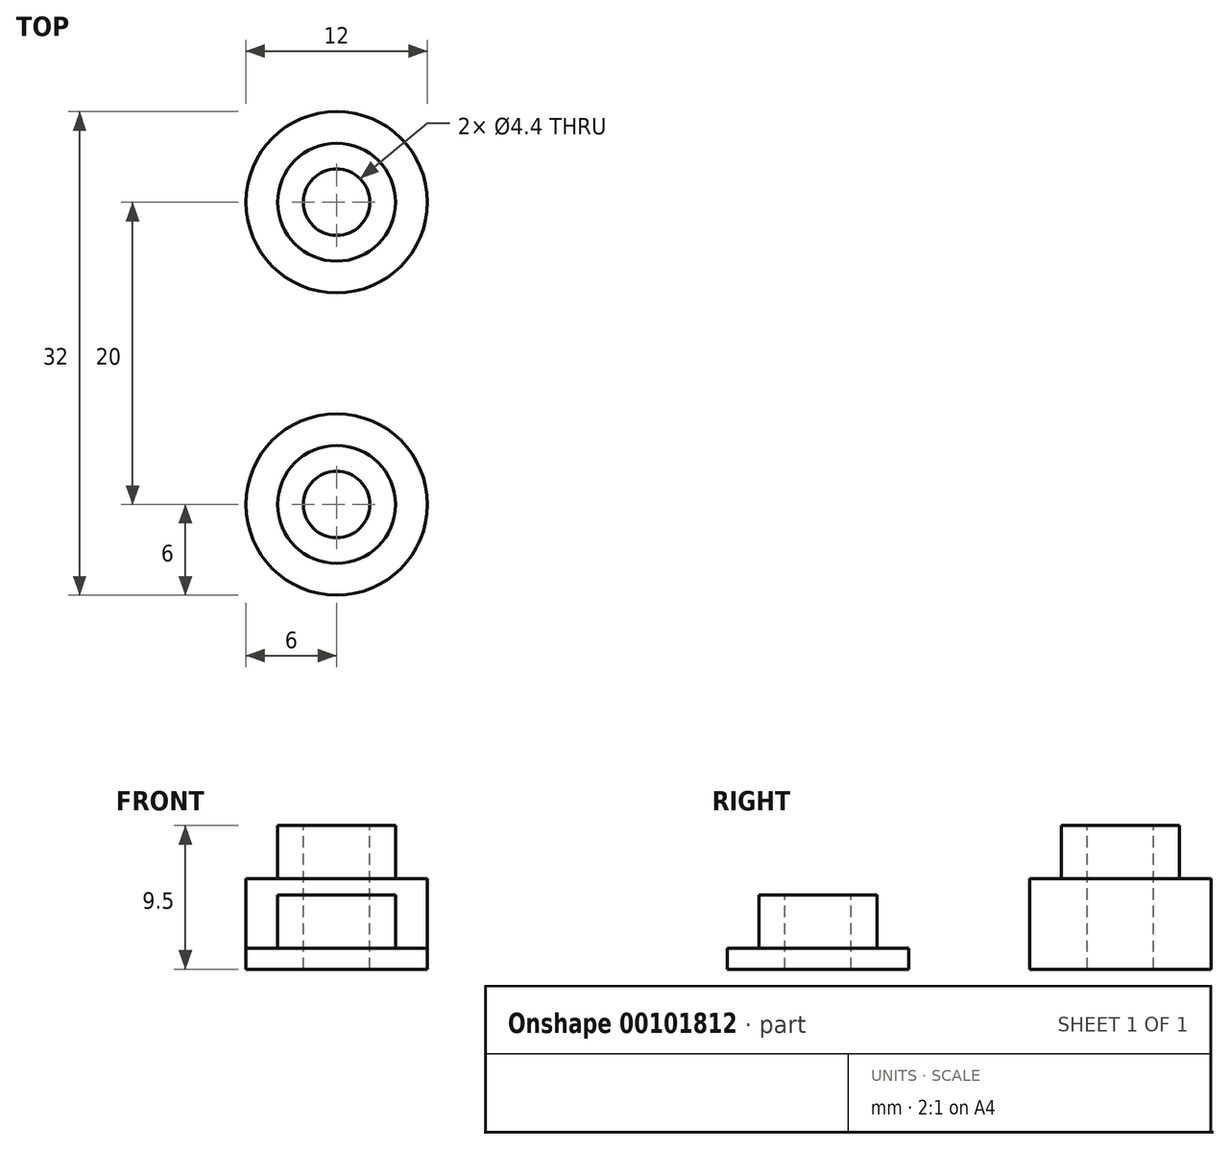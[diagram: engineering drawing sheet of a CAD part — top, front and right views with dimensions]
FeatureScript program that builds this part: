
annotation { "Feature Type Name" : "Feature", "Feature Type Description" : "" }
export const myFeature = defineFeature(function(context is Context, id is Id, definition is map)
    precondition{}
    {
        {
            var Q0;
            Q0=qCreatedBy(makeId("Top.planeOp"),FACE);
            var sketch = newSketch(context, id + "F0", { "sketchPlane" : qUnion([Q0])});
            skCircle(sketch, "E0", {"center": v(0, 0) * mm, "radius": 6 * mm});
            skSolve(sketch);
        }
        {
            var Q0;
            Q0=makeQuery(id+"F0.imprint","IMPRINT",FACE,{"disambiguationData":[TD([[makeQuery(id+"F0.imprint","IMPRINT",EDGE,{"derivedFrom":sQuery(id+"F0.wireOp",EDGE,"E0")}),1.0]])]});
            extrude(context, id + "F1", {"entities" : qUnion([Q0]), "depth" : 1.4 * mm});
        }
        {
            var Q0;
            Q0=makeQuery(id+"F1.opExtrude","CAP_FACE",FACE,{"disambiguationData":[OSD([sQuery(id+"F0.wireOp",EDGE,"E0")])],"isStart":false});
            var sketch = newSketch(context, id + "F2", { "sketchPlane" : qUnion([Q0])});
            skCircle(sketch, "E1", {"center": v(0, 0) * mm, "radius": 3.9 * mm});
            skSolve(sketch);
        }
        {
            var Q0;
            Q0 = qSketchRegion(id + "F2", true);
            extrude(context, id + "F3", {"entities" : qUnion([Q0]), "operationType" : NewBodyOperationType.ADD, "depth" : 3.5 * mm});
        }
        {
            var Q0;
            Q0=makeQuery(id+"F3.opExtrude","CAP_FACE",FACE,{"disambiguationData":[OSD([sQuery(id+"F2.wireOp",EDGE,"E1")])],"isStart":false});
            var sketch = newSketch(context, id + "F4", { "sketchPlane" : qUnion([Q0])});
            skCircle(sketch, "E2", {"center": v(0, 0) * mm, "radius": 2.2 * mm});
            skSolve(sketch);
        }
        {
            var Q0;
            Q0 = qSketchRegion(id + "F4", true);
            var Q1;
            Q1=makeQuery(id+"F1.opExtrude","CAP_FACE",FACE,{"disambiguationData":[OSD([sQuery(id+"F0.wireOp",EDGE,"E0")])],"isStart":true});
            extrude(context, id + "F5", {"entities" : qUnion([Q0]), "operationType" : NewBodyOperationType.REMOVE, "endBound" : BoundingType.UP_TO_SURFACE, "oppositeDirection" : true, "endBoundEntityFace" : qUnion([Q1]), "depth" : 25 * mm});
        }
        {
            var Q0;
            Q0=qCreatedBy(makeId("Top.planeOp"),FACE);
            var sketch = newSketch(context, id + "F6", { "sketchPlane" : qUnion([Q0])});
            skCircle(sketch, "E3", {"center": v(0, 20) * mm, "radius": 6 * mm});
            skSolve(sketch);
        }
        {
            var Q0;
            Q0=makeQuery(id+"F6.imprint","IMPRINT",FACE,{"disambiguationData":[TD([[makeQuery(id+"F6.imprint","IMPRINT",EDGE,{"derivedFrom":sQuery(id+"F6.wireOp",EDGE,"E3")}),1.0]])]});
            extrude(context, id + "F7", {"entities" : qUnion([Q0]), "depth" : 6 * mm});
        }
        {
            var Q0;
            Q0=makeQuery(id+"F7.opExtrude","CAP_FACE",FACE,{"disambiguationData":[OSD([sQuery(id+"F6.wireOp",EDGE,"E3")])],"isStart":false});
            var sketch = newSketch(context, id + "F8", { "sketchPlane" : qUnion([Q0])});
            skCircle(sketch, "E4", {"center": v(0, 20) * mm, "radius": 3.9 * mm});
            skSolve(sketch);
        }
        {
            var Q0;
            Q0=makeQuery(id+"F8.imprint","IMPRINT",FACE,{"disambiguationData":[TD([[makeQuery(id+"F8.imprint","IMPRINT",EDGE,{"derivedFrom":sQuery(id+"F8.wireOp",EDGE,"E4")}),1.0]])]});
            extrude(context, id + "F9", {"entities" : qUnion([Q0]), "operationType" : NewBodyOperationType.ADD, "depth" : 3.5 * mm});
        }
        {
            var Q0;
            Q0=makeQuery(id+"F9.opExtrude","CAP_FACE",FACE,{"disambiguationData":[OSD([sQuery(id+"F8.wireOp",EDGE,"E4")])],"isStart":false});
            var sketch = newSketch(context, id + "F10", { "sketchPlane" : qUnion([Q0])});
            skCircle(sketch, "E5", {"center": v(0, 20) * mm, "radius": 2.2 * mm});
            skSolve(sketch);
        }
        {
            var Q0;
            Q0 = qSketchRegion(id + "F10", true);
            var Q1;
            Q1=makeQuery(id+"F7.opExtrude","CAP_FACE",FACE,{"disambiguationData":[OSD([sQuery(id+"F6.wireOp",EDGE,"E3")])],"isStart":true});
            extrude(context, id + "F11", {"entities" : qUnion([Q0]), "operationType" : NewBodyOperationType.REMOVE, "endBound" : BoundingType.UP_TO_SURFACE, "oppositeDirection" : true, "endBoundEntityFace" : qUnion([Q1]), "depth" : 25 * mm});
        }
    });
